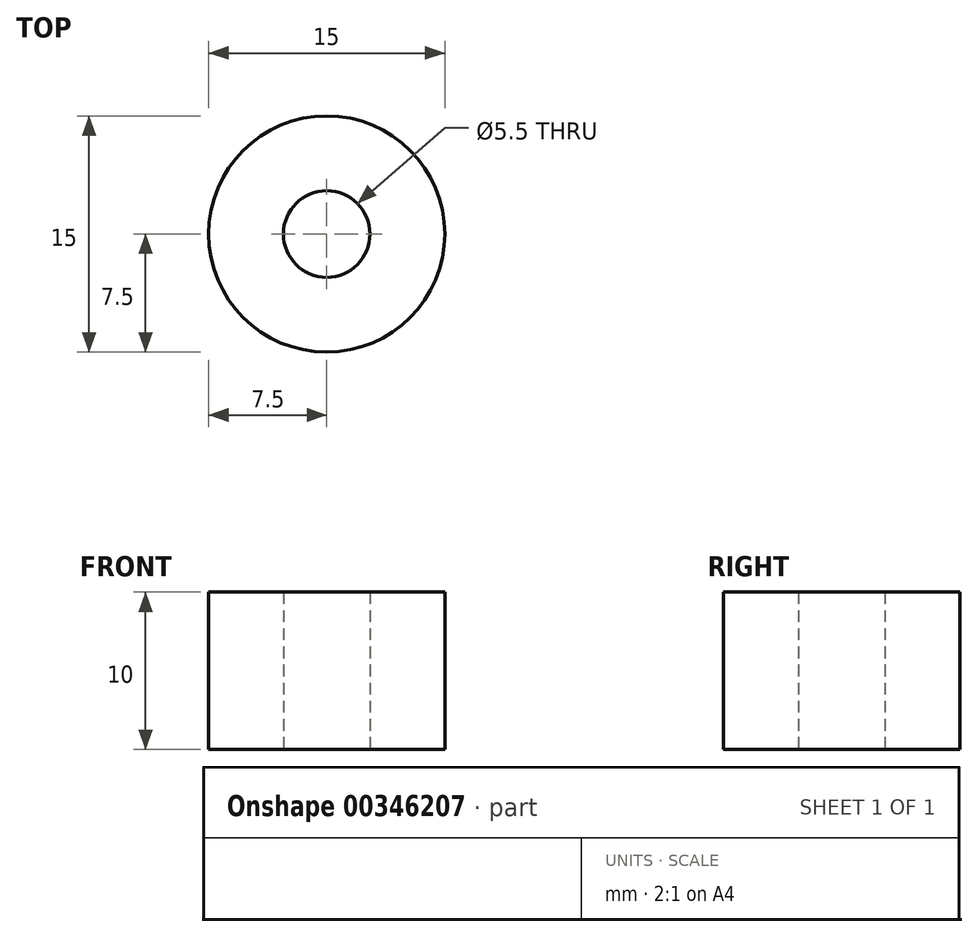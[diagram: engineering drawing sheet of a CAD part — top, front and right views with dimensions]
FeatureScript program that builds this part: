
annotation { "Feature Type Name" : "Feature", "Feature Type Description" : "" }
export const myFeature = defineFeature(function(context is Context, id is Id, definition is map)
    precondition{}
    {
        {
            var Q0;
            Q0=qCreatedBy(makeId("Top.planeOp"),FACE);
            var sketch = newSketch(context, id + "F0", { "sketchPlane" : qUnion([Q0])});
            skCircle(sketch, "E0", {"center": v(0, 0) * mm, "radius": 2.75 * mm});
            skCircle(sketch, "E1", {"center": v(0, 0) * mm, "radius": 7.5 * mm});
            skSolve(sketch);
        }
        {
            var Q0;
            Q0=makeQuery(id+"F0.imprint","IMPRINT",FACE,{"disambiguationData":[TD([[makeQuery(id+"F0.imprint","IMPRINT",EDGE,{"derivedFrom":sQuery(id+"F0.wireOp",EDGE,"E0")}),-1.0]])]});
            extrude(context, id + "F1", {"entities" : qUnion([Q0]), "depth" : 10 * mm});
        }
    });
